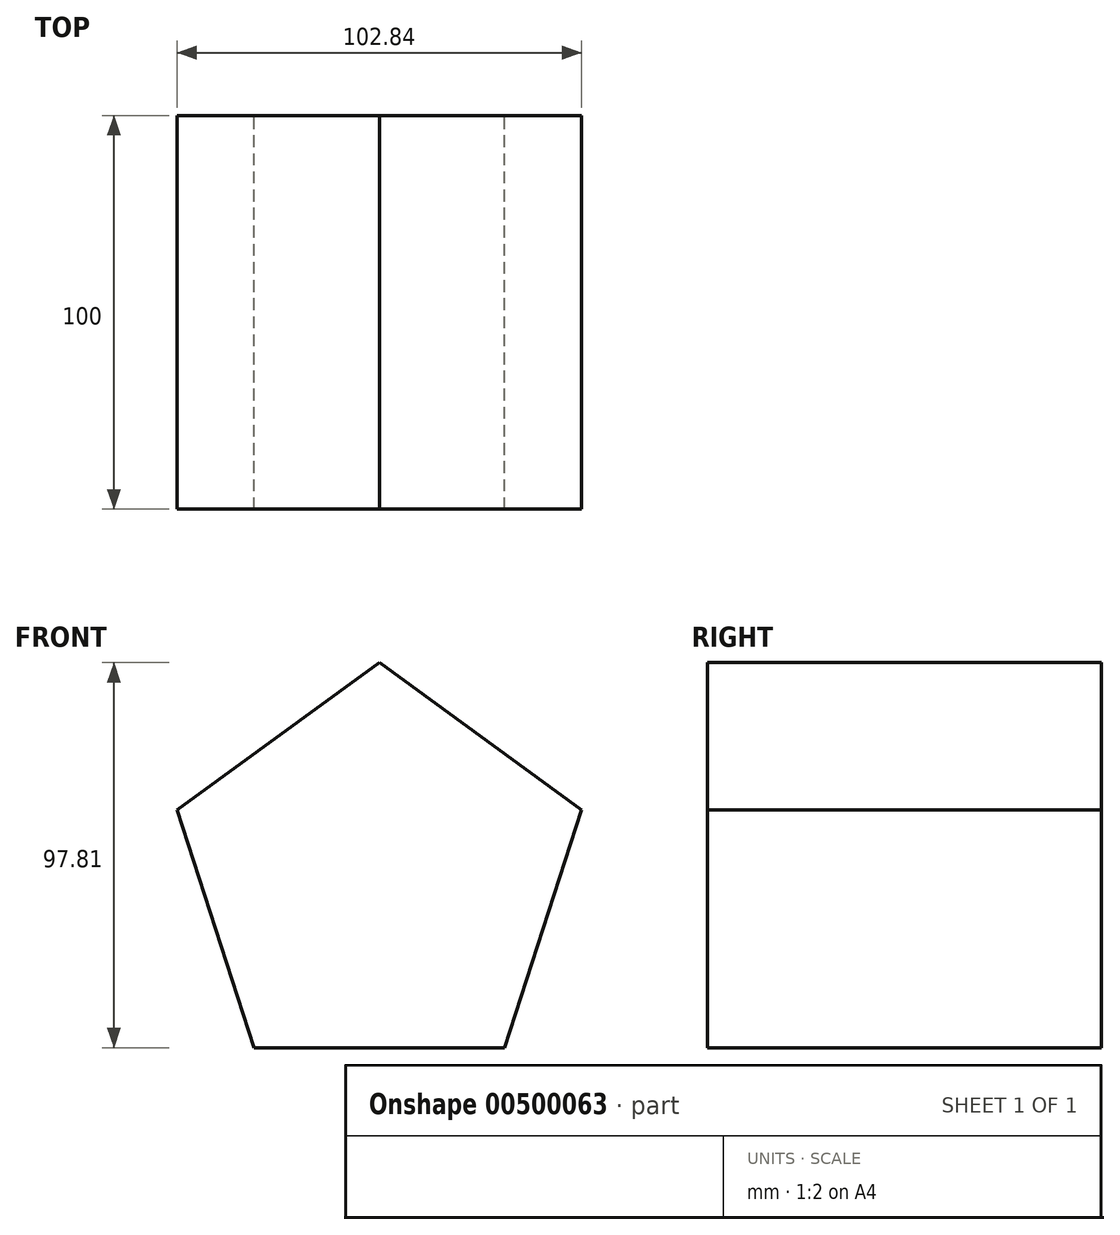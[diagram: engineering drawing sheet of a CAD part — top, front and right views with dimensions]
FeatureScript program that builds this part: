
annotation { "Feature Type Name" : "Feature", "Feature Type Description" : "" }
export const myFeature = defineFeature(function(context is Context, id is Id, definition is map)
    precondition{}
    {
        {
            var Q0;
            Q0=qCreatedBy(makeId("Front.planeOp"),FACE);
            var sketch = newSketch(context, id + "F0", { "sketchPlane" : qUnion([Q0])});
            skCircle(sketch, "E0.cCircle", {"center": v(0, 0) * mm, "radius": 54.07 * mm, "construction": true});
            skLineSegment(sketch, "E0.0", {"start": v(0, 54.07) * mm, "end": v(51.42, 16.7) * mm});
            skLineSegment(sketch, "E0.1", {"start": v(51.42, 16.7) * mm, "end": v(31.78, -43.74) * mm});
            skLineSegment(sketch, "E0.2", {"start": v(31.78, -43.74) * mm, "end": v(-31.78, -43.74) * mm});
            skLineSegment(sketch, "E0.3", {"start": v(-31.78, -43.74) * mm, "end": v(-51.42, 16.7) * mm});
            skLineSegment(sketch, "E0.4", {"start": v(-51.42, 16.7) * mm, "end": v(0, 54.07) * mm});
            skSolve(sketch);
        }
        {
            var Q0;
            Q0=makeQuery(id+"F0.imprint","IMPRINT",FACE,{"disambiguationData":[TD([[makeQuery(id+"F0.imprint","IMPRINT",EDGE,{"derivedFrom":sQuery(id+"F0.wireOp",EDGE,"E0.0")}),-1.0]])]});
            extrude(context, id + "F1", {"entities" : qUnion([Q0]), "depth" : 100 * mm, "symmetric" : true});
        }
    });
